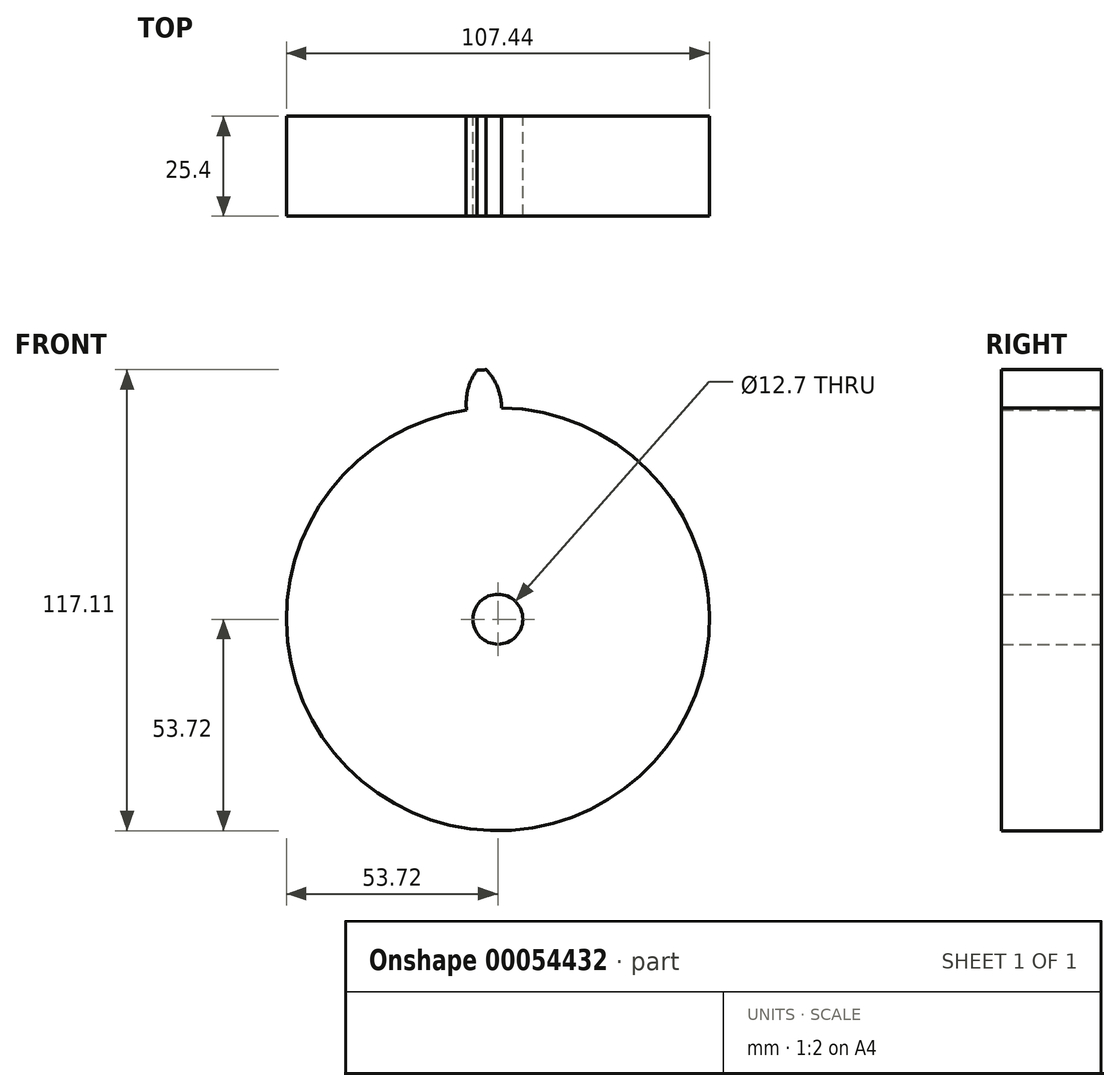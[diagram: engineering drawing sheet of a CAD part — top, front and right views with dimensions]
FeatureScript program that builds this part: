
annotation { "Feature Type Name" : "Feature", "Feature Type Description" : "" }
export const myFeature = defineFeature(function(context is Context, id is Id, definition is map)
    precondition{}
    {
        {
            var Q0;
            Q0=qCreatedBy(makeId("Front.planeOp"),FACE);
            var sketch = newSketch(context, id + "F0", { "sketchPlane" : qUnion([Q0])});
            skCircle(sketch, "E0", {"center": v(0, 0) * mm, "radius": 63.5 * mm, "construction": true});
            skCircle(sketch, "E1", {"center": v(0, 0) * mm, "radius": 58.67 * mm, "construction": true});
            skCircle(sketch, "E2", {"center": v(0, 0) * mm, "radius": 53.72 * mm});
            skLineSegment(sketch, "E3", {"start": v(0, 0) * mm, "end": v(0, 175.81) * mm, "construction": true});
            skLineSegment(sketch, "E4", {"start": v(0, 0) * mm, "end": v(-11.52, 175.81) * mm, "construction": true});
            skLineSegment(sketch, "E5", {"start": v(0, 58.67) * mm, "end": v(-79.4, 58.67) * mm, "construction": true});
            skLineSegment(sketch, "E6", {"start": v(0, 58.67) * mm, "end": v(-79.4, 29.77) * mm, "construction": true});
            skCircle(sketch, "E7", {"center": v(0, 0) * mm, "radius": 55.14 * mm, "construction": true});
            skCircle(sketch, "E8", {"center": v(0, 58.67) * mm, "radius": 14.6 * mm, "construction": true});
            skCircle(sketch, "E9", {"center": v(-13.63, 53.42) * mm, "radius": 14.6 * mm, "construction": true});
            skArc(sketch, "E10", {"start": v(0, 58.67) * mm, "mid": v(-1.24, 61.2) * mm, "end": v(-2.99, 63.43) * mm});
            skArc(sketch, "E11", {"start": v(0.97, 53.71) * mm, "mid": v(0.68, 56.23) * mm, "end": v(0, 58.67) * mm});
            skArc(sketch, "E12.MirrorCS", {"start": v(-7.66, 58.17) * mm, "mid": v(-6.76, 60.85) * mm, "end": v(-5.32, 63.28) * mm});
            skArc(sketch, "E13.MirrorCS", {"start": v(-7.98, 53.13) * mm, "mid": v(-8.02, 55.66) * mm, "end": v(-7.66, 58.17) * mm});
            skArc(sketch, "E14", {"start": v(-2.95, 63.4) * mm, "mid": v(-4.13, 63.34) * mm, "end": v(-5.32, 63.28) * mm});
            skCircle(sketch, "E15", {"center": v(0, 0) * mm, "radius": 6.35 * mm});
            skArc(sketch, "E16.1.0", {"start": v(-22.45, 54.2) * mm, "mid": v(-22.27, 57.03) * mm, "end": v(-21.51, 59.75) * mm});
            skArc(sketch, "E16.1.1", {"start": v(-21.45, 49.25) * mm, "mid": v(-22.15, 51.69) * mm, "end": v(-22.45, 54.2) * mm});
            skArc(sketch, "E16.1.2", {"start": v(-19.26, 60.47) * mm, "mid": v(-20.39, 60.1) * mm, "end": v(-21.51, 59.75) * mm});
            skArc(sketch, "E16.1.3", {"start": v(-15.19, 56.67) * mm, "mid": v(-17.04, 58.8) * mm, "end": v(-19.3, 60.5) * mm});
            skArc(sketch, "E16.1.4", {"start": v(-12.96, 52.13) * mm, "mid": v(-13.9, 54.5) * mm, "end": v(-15.19, 56.67) * mm});
            skArc(sketch, "E16.2.0", {"start": v(-35.72, 46.55) * mm, "mid": v(-36.27, 49.32) * mm, "end": v(-36.24, 52.14) * mm});
            skArc(sketch, "E16.2.1", {"start": v(-33.47, 42.02) * mm, "mid": v(-34.77, 44.2) * mm, "end": v(-35.72, 46.55) * mm});
            skArc(sketch, "E16.2.2", {"start": v(-34.25, 53.42) * mm, "mid": v(-35.25, 52.78) * mm, "end": v(-36.24, 52.14) * mm});
            skArc(sketch, "E16.2.3", {"start": v(-29.34, 50.81) * mm, "mid": v(-31.68, 52.39) * mm, "end": v(-34.3, 53.44) * mm});
            skArc(sketch, "E16.2.4", {"start": v(-26.01, 47) * mm, "mid": v(-27.52, 49.04) * mm, "end": v(-29.34, 50.81) * mm});
            skArc(sketch, "E16.3.0", {"start": v(-46.55, 35.72) * mm, "mid": v(-47.8, 38.25) * mm, "end": v(-48.5, 40.99) * mm});
            skArc(sketch, "E16.3.1", {"start": v(-43.2, 31.93) * mm, "mid": v(-45.03, 33.69) * mm, "end": v(-46.55, 35.72) * mm});
            skArc(sketch, "E16.3.2", {"start": v(-46.91, 42.74) * mm, "mid": v(-47.7, 41.86) * mm, "end": v(-48.5, 40.99) * mm});
            skArc(sketch, "E16.3.3", {"start": v(-41.49, 41.49) * mm, "mid": v(-44.16, 42.4) * mm, "end": v(-46.97, 42.74) * mm});
            skArc(sketch, "E16.3.4", {"start": v(-37.3, 38.67) * mm, "mid": v(-39.28, 40.24) * mm, "end": v(-41.49, 41.49) * mm});
            skArc(sketch, "E16.4.0", {"start": v(-54.2, 22.45) * mm, "mid": v(-56.07, 24.57) * mm, "end": v(-57.46, 27.04) * mm});
            skArc(sketch, "E16.4.1", {"start": v(-50, 19.66) * mm, "mid": v(-52.21, 20.89) * mm, "end": v(-54.2, 22.45) * mm});
            skArc(sketch, "E16.4.2", {"start": v(-56.38, 29.14) * mm, "mid": v(-56.92, 28.09) * mm, "end": v(-57.46, 27.04) * mm});
            skArc(sketch, "E16.4.3", {"start": v(-50.81, 29.34) * mm, "mid": v(-53.63, 29.53) * mm, "end": v(-56.43, 29.13) * mm});
            skArc(sketch, "E16.4.4", {"start": v(-46.03, 27.7) * mm, "mid": v(-48.36, 28.7) * mm, "end": v(-50.81, 29.34) * mm});
            skArc(sketch, "E16.5.0", {"start": v(-58.17, 7.66) * mm, "mid": v(-60.52, 9.22) * mm, "end": v(-62.5, 11.24) * mm});
            skArc(sketch, "E16.5.1", {"start": v(-53.38, 6.05) * mm, "mid": v(-55.84, 6.66) * mm, "end": v(-58.17, 7.66) * mm});
            skArc(sketch, "E16.5.2", {"start": v(-62, 13.55) * mm, "mid": v(-62.25, 12.4) * mm, "end": v(-62.5, 11.24) * mm});
            skArc(sketch, "E16.5.3", {"start": v(-56.67, 15.19) * mm, "mid": v(-59.45, 14.64) * mm, "end": v(-62.04, 13.53) * mm});
            skArc(sketch, "E16.5.4", {"start": v(-51.63, 14.84) * mm, "mid": v(-54.14, 15.21) * mm, "end": v(-56.67, 15.19) * mm});
            skArc(sketch, "E16.6.0", {"start": v(-58.17, -7.66) * mm, "mid": v(-60.85, -6.76) * mm, "end": v(-63.28, -5.32) * mm});
            skArc(sketch, "E16.6.1", {"start": v(-53.13, -7.98) * mm, "mid": v(-55.66, -8.02) * mm, "end": v(-58.17, -7.66) * mm});
            skArc(sketch, "E16.6.2", {"start": v(-63.4, -2.95) * mm, "mid": v(-63.34, -4.13) * mm, "end": v(-63.28, -5.32) * mm});
            skArc(sketch, "E16.6.3", {"start": v(-58.67, 0) * mm, "mid": v(-61.2, -1.24) * mm, "end": v(-63.43, -2.99) * mm});
            skArc(sketch, "E16.6.4", {"start": v(-53.71, 0.97) * mm, "mid": v(-56.23, 0.68) * mm, "end": v(-58.67, 0) * mm});
            skArc(sketch, "E16.7.0", {"start": v(-54.2, -22.45) * mm, "mid": v(-57.03, -22.27) * mm, "end": v(-59.75, -21.51) * mm});
            skArc(sketch, "E16.7.1", {"start": v(-49.25, -21.45) * mm, "mid": v(-51.69, -22.15) * mm, "end": v(-54.2, -22.45) * mm});
            skArc(sketch, "E16.7.2", {"start": v(-60.47, -19.26) * mm, "mid": v(-60.1, -20.39) * mm, "end": v(-59.75, -21.51) * mm});
            skArc(sketch, "E16.7.3", {"start": v(-56.67, -15.19) * mm, "mid": v(-58.8, -17.04) * mm, "end": v(-60.5, -19.3) * mm});
            skArc(sketch, "E16.7.4", {"start": v(-52.13, -12.96) * mm, "mid": v(-54.5, -13.9) * mm, "end": v(-56.67, -15.19) * mm});
            skArc(sketch, "E16.8.0", {"start": v(-46.55, -35.72) * mm, "mid": v(-49.32, -36.27) * mm, "end": v(-52.14, -36.24) * mm});
            skArc(sketch, "E16.8.1", {"start": v(-42.02, -33.47) * mm, "mid": v(-44.2, -34.77) * mm, "end": v(-46.55, -35.72) * mm});
            skArc(sketch, "E16.8.2", {"start": v(-53.42, -34.25) * mm, "mid": v(-52.78, -35.25) * mm, "end": v(-52.14, -36.24) * mm});
            skArc(sketch, "E16.8.3", {"start": v(-50.81, -29.34) * mm, "mid": v(-52.39, -31.68) * mm, "end": v(-53.44, -34.3) * mm});
            skArc(sketch, "E16.8.4", {"start": v(-47, -26.01) * mm, "mid": v(-49.04, -27.52) * mm, "end": v(-50.81, -29.34) * mm});
            skArc(sketch, "E16.9.0", {"start": v(-35.72, -46.55) * mm, "mid": v(-38.25, -47.8) * mm, "end": v(-40.99, -48.5) * mm});
            skArc(sketch, "E16.9.1", {"start": v(-31.93, -43.2) * mm, "mid": v(-33.69, -45.03) * mm, "end": v(-35.72, -46.55) * mm});
            skArc(sketch, "E16.9.2", {"start": v(-42.74, -46.91) * mm, "mid": v(-41.86, -47.7) * mm, "end": v(-40.99, -48.5) * mm});
            skArc(sketch, "E16.9.3", {"start": v(-41.49, -41.49) * mm, "mid": v(-42.4, -44.16) * mm, "end": v(-42.74, -46.97) * mm});
            skArc(sketch, "E16.9.4", {"start": v(-38.67, -37.3) * mm, "mid": v(-40.24, -39.28) * mm, "end": v(-41.49, -41.49) * mm});
            skArc(sketch, "E16.10.0", {"start": v(-22.45, -54.2) * mm, "mid": v(-24.57, -56.07) * mm, "end": v(-27.04, -57.46) * mm});
            skArc(sketch, "E16.10.1", {"start": v(-19.66, -50) * mm, "mid": v(-20.89, -52.21) * mm, "end": v(-22.45, -54.2) * mm});
            skArc(sketch, "E16.10.2", {"start": v(-29.14, -56.38) * mm, "mid": v(-28.09, -56.92) * mm, "end": v(-27.04, -57.46) * mm});
            skArc(sketch, "E16.10.3", {"start": v(-29.34, -50.81) * mm, "mid": v(-29.53, -53.63) * mm, "end": v(-29.13, -56.43) * mm});
            skArc(sketch, "E16.10.4", {"start": v(-27.7, -46.03) * mm, "mid": v(-28.7, -48.36) * mm, "end": v(-29.34, -50.81) * mm});
            skArc(sketch, "E16.11.0", {"start": v(-7.66, -58.17) * mm, "mid": v(-9.22, -60.52) * mm, "end": v(-11.24, -62.5) * mm});
            skArc(sketch, "E16.11.1", {"start": v(-6.05, -53.38) * mm, "mid": v(-6.66, -55.84) * mm, "end": v(-7.66, -58.17) * mm});
            skArc(sketch, "E16.11.2", {"start": v(-13.55, -62) * mm, "mid": v(-12.4, -62.25) * mm, "end": v(-11.24, -62.5) * mm});
            skArc(sketch, "E16.11.3", {"start": v(-15.19, -56.67) * mm, "mid": v(-14.64, -59.45) * mm, "end": v(-13.53, -62.04) * mm});
            skArc(sketch, "E16.11.4", {"start": v(-14.84, -51.63) * mm, "mid": v(-15.21, -54.14) * mm, "end": v(-15.19, -56.67) * mm});
            skArc(sketch, "E16.12.0", {"start": v(7.66, -58.17) * mm, "mid": v(6.76, -60.85) * mm, "end": v(5.32, -63.28) * mm});
            skArc(sketch, "E16.12.1", {"start": v(7.98, -53.13) * mm, "mid": v(8.02, -55.66) * mm, "end": v(7.66, -58.17) * mm});
            skArc(sketch, "E16.12.2", {"start": v(2.95, -63.4) * mm, "mid": v(4.13, -63.34) * mm, "end": v(5.32, -63.28) * mm});
            skArc(sketch, "E16.12.3", {"start": v(0, -58.67) * mm, "mid": v(1.24, -61.2) * mm, "end": v(2.99, -63.43) * mm});
            skArc(sketch, "E16.12.4", {"start": v(-0.97, -53.71) * mm, "mid": v(-0.68, -56.23) * mm, "end": v(0, -58.67) * mm});
            skArc(sketch, "E16.13.0", {"start": v(22.45, -54.2) * mm, "mid": v(22.27, -57.03) * mm, "end": v(21.51, -59.75) * mm});
            skArc(sketch, "E16.13.1", {"start": v(21.45, -49.25) * mm, "mid": v(22.15, -51.69) * mm, "end": v(22.45, -54.2) * mm});
            skArc(sketch, "E16.13.2", {"start": v(19.26, -60.47) * mm, "mid": v(20.39, -60.1) * mm, "end": v(21.51, -59.75) * mm});
            skArc(sketch, "E16.13.3", {"start": v(15.19, -56.67) * mm, "mid": v(17.04, -58.8) * mm, "end": v(19.3, -60.5) * mm});
            skArc(sketch, "E16.13.4", {"start": v(12.96, -52.13) * mm, "mid": v(13.9, -54.5) * mm, "end": v(15.19, -56.67) * mm});
            skArc(sketch, "E16.14.0", {"start": v(35.72, -46.55) * mm, "mid": v(36.27, -49.32) * mm, "end": v(36.24, -52.14) * mm});
            skArc(sketch, "E16.14.1", {"start": v(33.47, -42.02) * mm, "mid": v(34.77, -44.2) * mm, "end": v(35.72, -46.55) * mm});
            skArc(sketch, "E16.14.2", {"start": v(34.25, -53.42) * mm, "mid": v(35.25, -52.78) * mm, "end": v(36.24, -52.14) * mm});
            skArc(sketch, "E16.14.3", {"start": v(29.34, -50.81) * mm, "mid": v(31.68, -52.39) * mm, "end": v(34.3, -53.44) * mm});
            skArc(sketch, "E16.14.4", {"start": v(26.01, -47) * mm, "mid": v(27.52, -49.04) * mm, "end": v(29.34, -50.81) * mm});
            skArc(sketch, "E16.15.0", {"start": v(46.55, -35.72) * mm, "mid": v(47.8, -38.25) * mm, "end": v(48.5, -40.99) * mm});
            skArc(sketch, "E16.15.1", {"start": v(43.2, -31.93) * mm, "mid": v(45.03, -33.69) * mm, "end": v(46.55, -35.72) * mm});
            skArc(sketch, "E16.15.2", {"start": v(46.91, -42.74) * mm, "mid": v(47.7, -41.86) * mm, "end": v(48.5, -40.99) * mm});
            skArc(sketch, "E16.15.3", {"start": v(41.49, -41.49) * mm, "mid": v(44.16, -42.4) * mm, "end": v(46.97, -42.74) * mm});
            skArc(sketch, "E16.15.4", {"start": v(37.3, -38.67) * mm, "mid": v(39.28, -40.24) * mm, "end": v(41.49, -41.49) * mm});
            skArc(sketch, "E16.16.0", {"start": v(54.2, -22.45) * mm, "mid": v(56.07, -24.57) * mm, "end": v(57.46, -27.04) * mm});
            skArc(sketch, "E16.16.1", {"start": v(50, -19.66) * mm, "mid": v(52.21, -20.89) * mm, "end": v(54.2, -22.45) * mm});
            skArc(sketch, "E16.16.2", {"start": v(56.38, -29.14) * mm, "mid": v(56.92, -28.09) * mm, "end": v(57.46, -27.04) * mm});
            skArc(sketch, "E16.16.3", {"start": v(50.81, -29.34) * mm, "mid": v(53.63, -29.53) * mm, "end": v(56.43, -29.13) * mm});
            skArc(sketch, "E16.16.4", {"start": v(46.03, -27.7) * mm, "mid": v(48.36, -28.7) * mm, "end": v(50.81, -29.34) * mm});
            skArc(sketch, "E16.17.0", {"start": v(58.17, -7.66) * mm, "mid": v(60.52, -9.22) * mm, "end": v(62.5, -11.24) * mm});
            skArc(sketch, "E16.17.1", {"start": v(53.38, -6.05) * mm, "mid": v(55.84, -6.66) * mm, "end": v(58.17, -7.66) * mm});
            skArc(sketch, "E16.17.2", {"start": v(62, -13.55) * mm, "mid": v(62.25, -12.4) * mm, "end": v(62.5, -11.24) * mm});
            skArc(sketch, "E16.17.3", {"start": v(56.67, -15.19) * mm, "mid": v(59.45, -14.64) * mm, "end": v(62.04, -13.53) * mm});
            skArc(sketch, "E16.17.4", {"start": v(51.63, -14.84) * mm, "mid": v(54.14, -15.21) * mm, "end": v(56.67, -15.19) * mm});
            skArc(sketch, "E16.18.0", {"start": v(58.17, 7.66) * mm, "mid": v(60.85, 6.76) * mm, "end": v(63.28, 5.32) * mm});
            skArc(sketch, "E16.18.1", {"start": v(53.13, 7.98) * mm, "mid": v(55.66, 8.02) * mm, "end": v(58.17, 7.66) * mm});
            skArc(sketch, "E16.18.2", {"start": v(63.4, 2.95) * mm, "mid": v(63.34, 4.13) * mm, "end": v(63.28, 5.32) * mm});
            skArc(sketch, "E16.18.3", {"start": v(58.67, 0) * mm, "mid": v(61.2, 1.24) * mm, "end": v(63.43, 2.99) * mm});
            skArc(sketch, "E16.18.4", {"start": v(53.71, -0.97) * mm, "mid": v(56.23, -0.68) * mm, "end": v(58.67, 0) * mm});
            skArc(sketch, "E16.19.0", {"start": v(54.2, 22.45) * mm, "mid": v(57.03, 22.27) * mm, "end": v(59.75, 21.51) * mm});
            skArc(sketch, "E16.19.1", {"start": v(49.25, 21.45) * mm, "mid": v(51.69, 22.15) * mm, "end": v(54.2, 22.45) * mm});
            skArc(sketch, "E16.19.2", {"start": v(60.47, 19.26) * mm, "mid": v(60.1, 20.39) * mm, "end": v(59.75, 21.51) * mm});
            skArc(sketch, "E16.19.3", {"start": v(56.67, 15.19) * mm, "mid": v(58.8, 17.04) * mm, "end": v(60.5, 19.3) * mm});
            skArc(sketch, "E16.19.4", {"start": v(52.13, 12.96) * mm, "mid": v(54.5, 13.9) * mm, "end": v(56.67, 15.19) * mm});
            skArc(sketch, "E16.20.0", {"start": v(46.55, 35.72) * mm, "mid": v(49.32, 36.27) * mm, "end": v(52.14, 36.24) * mm});
            skArc(sketch, "E16.20.1", {"start": v(42.02, 33.47) * mm, "mid": v(44.2, 34.77) * mm, "end": v(46.55, 35.72) * mm});
            skArc(sketch, "E16.20.2", {"start": v(53.42, 34.25) * mm, "mid": v(52.78, 35.25) * mm, "end": v(52.14, 36.24) * mm});
            skArc(sketch, "E16.20.3", {"start": v(50.81, 29.34) * mm, "mid": v(52.39, 31.68) * mm, "end": v(53.44, 34.3) * mm});
            skArc(sketch, "E16.20.4", {"start": v(47, 26.01) * mm, "mid": v(49.04, 27.52) * mm, "end": v(50.81, 29.34) * mm});
            skArc(sketch, "E16.21.0", {"start": v(35.72, 46.55) * mm, "mid": v(38.25, 47.8) * mm, "end": v(40.99, 48.5) * mm});
            skArc(sketch, "E16.21.1", {"start": v(31.93, 43.2) * mm, "mid": v(33.69, 45.03) * mm, "end": v(35.72, 46.55) * mm});
            skArc(sketch, "E16.21.2", {"start": v(42.74, 46.91) * mm, "mid": v(41.86, 47.7) * mm, "end": v(40.99, 48.5) * mm});
            skArc(sketch, "E16.21.3", {"start": v(41.49, 41.49) * mm, "mid": v(42.4, 44.16) * mm, "end": v(42.74, 46.97) * mm});
            skArc(sketch, "E16.21.4", {"start": v(38.67, 37.3) * mm, "mid": v(40.24, 39.28) * mm, "end": v(41.49, 41.49) * mm});
            skArc(sketch, "E16.22.0", {"start": v(22.45, 54.2) * mm, "mid": v(24.57, 56.07) * mm, "end": v(27.04, 57.46) * mm});
            skArc(sketch, "E16.22.1", {"start": v(19.66, 50) * mm, "mid": v(20.89, 52.21) * mm, "end": v(22.45, 54.2) * mm});
            skArc(sketch, "E16.22.2", {"start": v(29.14, 56.38) * mm, "mid": v(28.09, 56.92) * mm, "end": v(27.04, 57.46) * mm});
            skArc(sketch, "E16.22.3", {"start": v(29.34, 50.81) * mm, "mid": v(29.53, 53.63) * mm, "end": v(29.13, 56.43) * mm});
            skArc(sketch, "E16.22.4", {"start": v(27.7, 46.03) * mm, "mid": v(28.7, 48.36) * mm, "end": v(29.34, 50.81) * mm});
            skArc(sketch, "E16.23.0", {"start": v(7.66, 58.17) * mm, "mid": v(9.22, 60.52) * mm, "end": v(11.24, 62.5) * mm});
            skArc(sketch, "E16.23.1", {"start": v(6.05, 53.38) * mm, "mid": v(6.66, 55.84) * mm, "end": v(7.66, 58.17) * mm});
            skArc(sketch, "E16.23.2", {"start": v(13.55, 62) * mm, "mid": v(12.4, 62.25) * mm, "end": v(11.24, 62.5) * mm});
            skArc(sketch, "E16.23.3", {"start": v(15.19, 56.67) * mm, "mid": v(14.64, 59.45) * mm, "end": v(13.53, 62.04) * mm});
            skArc(sketch, "E16.23.4", {"start": v(14.84, 51.63) * mm, "mid": v(15.21, 54.14) * mm, "end": v(15.19, 56.67) * mm});
            skSolve(sketch);
        }
        {
            var Q0;
            {var subQ0=sQuery(id+"F0.wireOp",EDGE,"E2");var subQ1=makeQuery(id+"F0.imprint","INTERSECT",VERTEX,{"derivedFrom":[subQ0,sQuery(id+"F0.wireOp",EDGE,"E11")]});Q0=makeQuery(id+"F0.imprint","IMPRINT",FACE,{"disambiguationData":[TD([[makeQuery(id+"F0.imprint","IMPRINT",EDGE,{"disambiguationData":[TD([[subQ1,-1.0]])],"derivedFrom":subQ0}),1.0]])]});}
            var Q1;
            {var subQ0=sQuery(id+"F0.wireOp",EDGE,"E11");Q1=makeQuery(id+"F0.imprint","IMPRINT",FACE,{"disambiguationData":[TD([[makeQuery(id+"F0.imprint","IMPRINT",EDGE,{"derivedFrom":subQ0}),1.0]])]});}
            var Q2;
            Q2=makeQuery(id+"F0.imprint","IMPRINT",FACE,{"disambiguationData":[TD([[makeQuery(id+"F0.imprint","IMPRINT",EDGE,{"derivedFrom":sQuery(id+"F0.wireOp",EDGE,"E16.1.0")}),-1.0]])]});
            var Q3;
            Q3=makeQuery(id+"F0.imprint","IMPRINT",FACE,{"disambiguationData":[TD([[makeQuery(id+"F0.imprint","IMPRINT",EDGE,{"derivedFrom":sQuery(id+"F0.wireOp",EDGE,"E16.2.0")}),-1.0]])]});
            var Q4;
            Q4=makeQuery(id+"F0.imprint","IMPRINT",FACE,{"disambiguationData":[TD([[makeQuery(id+"F0.imprint","IMPRINT",EDGE,{"derivedFrom":sQuery(id+"F0.wireOp",EDGE,"E16.3.0")}),-1.0]])]});
            var Q5;
            Q5=makeQuery(id+"F0.imprint","IMPRINT",FACE,{"disambiguationData":[TD([[makeQuery(id+"F0.imprint","IMPRINT",EDGE,{"derivedFrom":sQuery(id+"F0.wireOp",EDGE,"E16.4.0")}),-1.0]])]});
            var Q6;
            Q6=makeQuery(id+"F0.imprint","IMPRINT",FACE,{"disambiguationData":[TD([[makeQuery(id+"F0.imprint","IMPRINT",EDGE,{"derivedFrom":sQuery(id+"F0.wireOp",EDGE,"E16.5.0")}),-1.0]])]});
            var Q7;
            Q7=makeQuery(id+"F0.imprint","IMPRINT",FACE,{"disambiguationData":[TD([[makeQuery(id+"F0.imprint","IMPRINT",EDGE,{"derivedFrom":sQuery(id+"F0.wireOp",EDGE,"E16.6.0")}),-1.0]])]});
            var Q8;
            Q8=makeQuery(id+"F0.imprint","IMPRINT",FACE,{"disambiguationData":[TD([[makeQuery(id+"F0.imprint","IMPRINT",EDGE,{"derivedFrom":sQuery(id+"F0.wireOp",EDGE,"E16.7.0")}),-1.0]])]});
            var Q9;
            Q9=makeQuery(id+"F0.imprint","IMPRINT",FACE,{"disambiguationData":[TD([[makeQuery(id+"F0.imprint","IMPRINT",EDGE,{"derivedFrom":sQuery(id+"F0.wireOp",EDGE,"E16.8.0")}),-1.0]])]});
            var Q10;
            Q10=makeQuery(id+"F0.imprint","IMPRINT",FACE,{"disambiguationData":[TD([[makeQuery(id+"F0.imprint","IMPRINT",EDGE,{"derivedFrom":sQuery(id+"F0.wireOp",EDGE,"E16.9.0")}),-1.0]])]});
            var Q11;
            Q11=makeQuery(id+"F0.imprint","IMPRINT",FACE,{"disambiguationData":[TD([[makeQuery(id+"F0.imprint","IMPRINT",EDGE,{"derivedFrom":sQuery(id+"F0.wireOp",EDGE,"E16.10.0")}),-1.0]])]});
            var Q12;
            Q12=makeQuery(id+"F0.imprint","IMPRINT",FACE,{"disambiguationData":[TD([[makeQuery(id+"F0.imprint","IMPRINT",EDGE,{"derivedFrom":sQuery(id+"F0.wireOp",EDGE,"E16.11.0")}),-1.0]])]});
            var Q13;
            Q13=makeQuery(id+"F0.imprint","IMPRINT",FACE,{"disambiguationData":[TD([[makeQuery(id+"F0.imprint","IMPRINT",EDGE,{"derivedFrom":sQuery(id+"F0.wireOp",EDGE,"E16.12.0")}),-1.0]])]});
            var Q14;
            Q14=makeQuery(id+"F0.imprint","IMPRINT",FACE,{"disambiguationData":[TD([[makeQuery(id+"F0.imprint","IMPRINT",EDGE,{"derivedFrom":sQuery(id+"F0.wireOp",EDGE,"E16.13.0")}),-1.0]])]});
            var Q15;
            Q15=makeQuery(id+"F0.imprint","IMPRINT",FACE,{"disambiguationData":[TD([[makeQuery(id+"F0.imprint","IMPRINT",EDGE,{"derivedFrom":sQuery(id+"F0.wireOp",EDGE,"E16.14.0")}),-1.0]])]});
            var Q16;
            Q16=makeQuery(id+"F0.imprint","IMPRINT",FACE,{"disambiguationData":[TD([[makeQuery(id+"F0.imprint","IMPRINT",EDGE,{"derivedFrom":sQuery(id+"F0.wireOp",EDGE,"E16.15.0")}),-1.0]])]});
            var Q17;
            Q17=makeQuery(id+"F0.imprint","IMPRINT",FACE,{"disambiguationData":[TD([[makeQuery(id+"F0.imprint","IMPRINT",EDGE,{"derivedFrom":sQuery(id+"F0.wireOp",EDGE,"E16.16.0")}),-1.0]])]});
            var Q18;
            Q18=makeQuery(id+"F0.imprint","IMPRINT",FACE,{"disambiguationData":[TD([[makeQuery(id+"F0.imprint","IMPRINT",EDGE,{"derivedFrom":sQuery(id+"F0.wireOp",EDGE,"E16.17.0")}),-1.0]])]});
            var Q19;
            Q19=makeQuery(id+"F0.imprint","IMPRINT",FACE,{"disambiguationData":[TD([[makeQuery(id+"F0.imprint","IMPRINT",EDGE,{"derivedFrom":sQuery(id+"F0.wireOp",EDGE,"E16.18.0")}),-1.0]])]});
            var Q20;
            Q20=makeQuery(id+"F0.imprint","IMPRINT",FACE,{"disambiguationData":[TD([[makeQuery(id+"F0.imprint","IMPRINT",EDGE,{"derivedFrom":sQuery(id+"F0.wireOp",EDGE,"E16.19.0")}),-1.0]])]});
            var Q21;
            Q21=makeQuery(id+"F0.imprint","IMPRINT",FACE,{"disambiguationData":[TD([[makeQuery(id+"F0.imprint","IMPRINT",EDGE,{"derivedFrom":sQuery(id+"F0.wireOp",EDGE,"E16.20.0")}),-1.0]])]});
            var Q22;
            Q22=makeQuery(id+"F0.imprint","IMPRINT",FACE,{"disambiguationData":[TD([[makeQuery(id+"F0.imprint","IMPRINT",EDGE,{"derivedFrom":sQuery(id+"F0.wireOp",EDGE,"E16.21.0")}),-1.0]])]});
            var Q23;
            Q23=makeQuery(id+"F0.imprint","IMPRINT",FACE,{"disambiguationData":[TD([[makeQuery(id+"F0.imprint","IMPRINT",EDGE,{"derivedFrom":sQuery(id+"F0.wireOp",EDGE,"E16.22.0")}),-1.0]])]});
            var Q24;
            Q24=makeQuery(id+"F0.imprint","IMPRINT",FACE,{"disambiguationData":[TD([[makeQuery(id+"F0.imprint","IMPRINT",EDGE,{"derivedFrom":sQuery(id+"F0.wireOp",EDGE,"E16.23.0")}),-1.0]])]});
            extrude(context, id + "F1", {"entities" : qUnion([Q0, Q1, Q2, Q3, Q4, Q5, Q6, Q7, Q8, Q9, Q10, Q11, Q12, Q13, Q14, Q15, Q16, Q17, Q18, Q19, Q20, Q21, Q22, Q23, Q24]), "depth" : 25.4 * mm});
        }
    });
